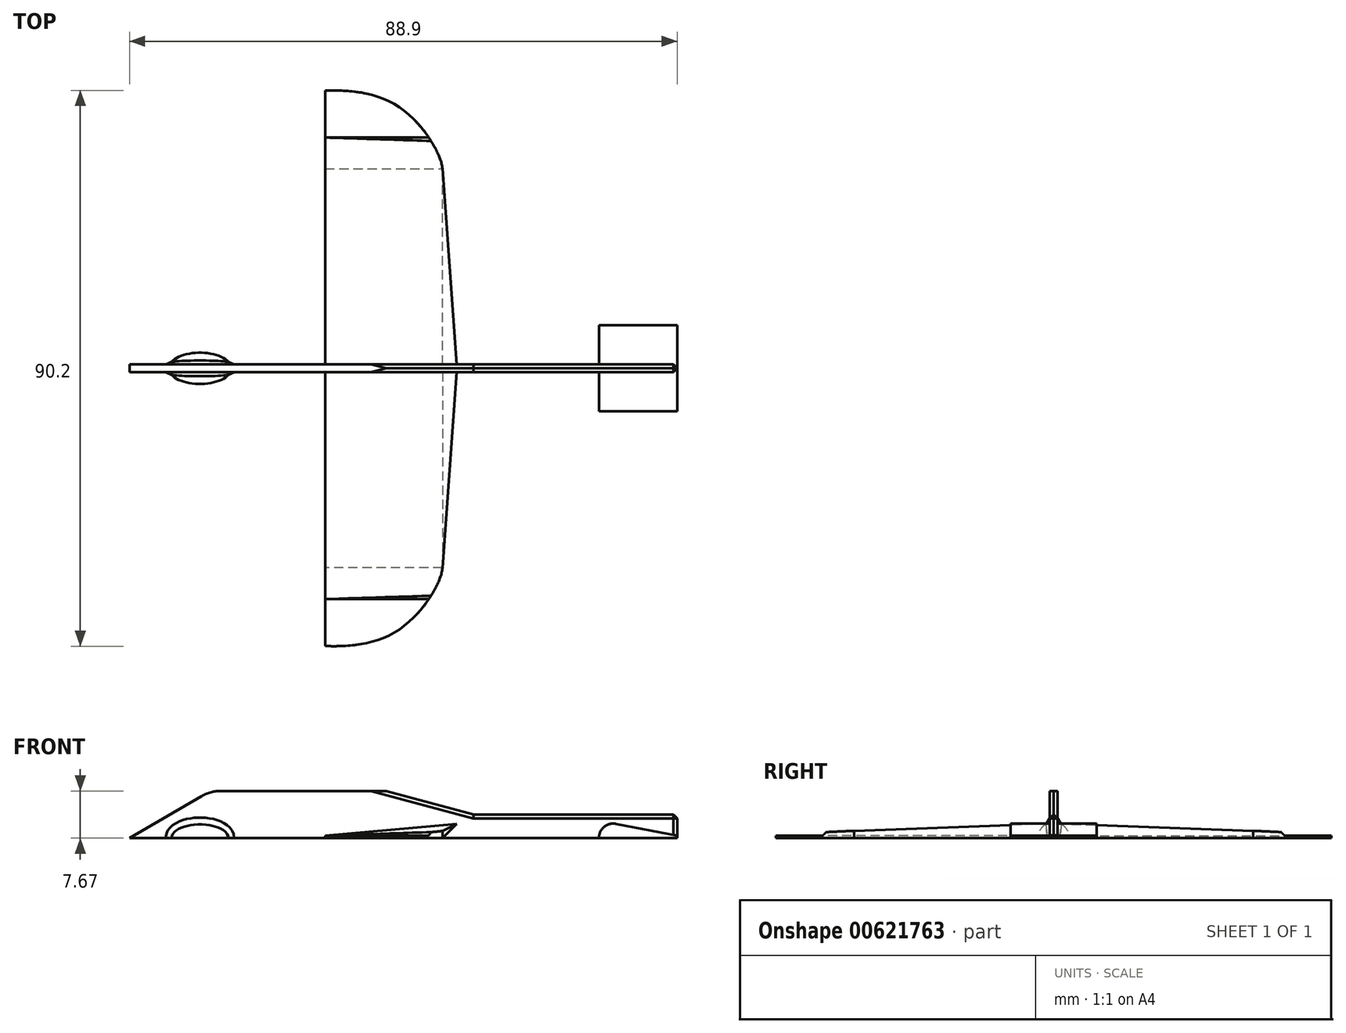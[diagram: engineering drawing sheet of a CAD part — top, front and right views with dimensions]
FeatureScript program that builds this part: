
annotation { "Feature Type Name" : "Feature", "Feature Type Description" : "" }
export const myFeature = defineFeature(function(context is Context, id is Id, definition is map)
    precondition{}
    {
        {
            var Q0;
            Q0=qCreatedBy(makeId("Front.planeOp"),FACE);
            cPlane(context, id + "F0", {"entities" : qUnion([Q0]), "cplaneType" : CPlaneType.OFFSET, "offset" : 0.64 * mm, "width" : 152.4 * mm, "height" : 152.4 * mm});
        }
        {
            var Q0;
            Q0=qCreatedBy(id+"F0.planeOp",FACE);
            var sketch = newSketch(context, id + "F1", { "sketchPlane" : qUnion([Q0])});
            skLineSegment(sketch, "E0", {"start": v(-19.05, 0) * mm, "end": v(0, 0) * mm});
            skLineSegment(sketch, "E1", {"start": v(0, 0) * mm, "end": v(2.29, 2.29) * mm});
            skLineSegment(sketch, "E2", {"start": v(-19.05, 0) * mm, "end": v(-19.05, 0.38) * mm});
            skLineSegment(sketch, "E3", {"start": v(-19.05, 0.38) * mm, "end": v(2.29, 2.29) * mm});
            skSolve(sketch);
        }
        {
            var Q0;
            Q0=qCreatedBy(id+"F0.planeOp",FACE);
            cPlane(context, id + "F2", {"entities" : qUnion([Q0]), "cplaneType" : CPlaneType.OFFSET, "offset" : 31.75 * mm, "width" : 152.4 * mm, "height" : 152.4 * mm});
        }
        {
            var Q0;
            Q0=qCreatedBy(id+"F2.planeOp",FACE);
            var sketch = newSketch(context, id + "F3", { "sketchPlane" : qUnion([Q0])});
            skLineSegment(sketch, "E4.bottom", {"start": v(0, 0) * mm, "end": v(-19.05, -0.05) * mm});
            skLineSegment(sketch, "E4.top", {"start": v(0, 1.14) * mm, "end": v(-19.05, 0.38) * mm});
            skLineSegment(sketch, "E4.left", {"start": v(0, 0) * mm, "end": v(0, 1.14) * mm});
            skLineSegment(sketch, "E4.right", {"start": v(-19.05, -0.05) * mm, "end": v(-19.05, 0.38) * mm});
            skSolve(sketch);
        }
        {
            var Q0;
            Q0 = qSketchRegion(id + "F1", true);
            var Q1;
            Q1 = qSketchRegion(id + "F3", true);
            loft(context, id + "F4", {"sheetProfilesArray" : [{ "sheetProfileEntities" : qUnion([Q0]) }, { "sheetProfileEntities" : qUnion([Q1]) }]});
        }
        {
            var Q0;
            Q0=qCreatedBy(makeId("Top.planeOp"),FACE);
            var sketch = newSketch(context, id + "F5", { "sketchPlane" : qUnion([Q0])});
            skLineSegment(sketch, "E5", {"start": v(-19.05, -32.38) * mm, "end": v(0, -32.38) * mm});
            skLineSegment(sketch, "E6", {"start": v(-19.05, -45.09) * mm, "end": v(-19.05, -32.38) * mm});
            skFitSpline(sketch, "E7", {"points": [v(-19.05, -45.09) * mm, v(-8.27, -43.16) * mm, v(0, -32.38) * mm], "startDerivative": vector(8.05, 0) * mm, "endDerivative": vector(1.04, 14.46) * mm});
            skLineSegment(sketch, "E8", {"start": v(-19.05, -45.09) * mm, "end": v(-21.64, -45.09) * mm, "construction": true});
            skLineSegment(sketch, "E9", {"start": v(-19.05, -32.38) * mm, "end": v(-8.27, -43.16) * mm, "construction": true});
            skSolve(sketch);
        }
        {
            var Q0;
            Q0 = qSketchRegion(id + "F5", true);
            var Q1;
            Q1=makeQuery(id+"F4.opLoft","MID_CAP_VERTEX",VERTEX,{"disambiguationData":[OSD([sQuery(id+"F3.wireOp",EDGE,"E4.top"),sQuery(id+"F3.wireOp",EDGE,"E4.right")])],"capPos":1.0});
            extrude(context, id + "F6", {"entities" : qUnion([Q0]), "operationType" : NewBodyOperationType.ADD, "endBound" : BoundingType.UP_TO_VERTEX, "depth" : 0.76 * mm, "endBoundEntityVertex" : qUnion([Q1]), "offsetDistance" : 25.4 * mm});
        }
        {
            var Q0;
            Q0=qCreatedBy(makeId("Front.planeOp"),FACE);
            var sketch = newSketch(context, id + "F7", { "sketchPlane" : qUnion([Q0])});
            skLineSegment(sketch, "E10", {"start": v(0, 0) * mm, "end": v(-50.8, 0) * mm});
            skLineSegment(sketch, "E11", {"start": v(-50.8, 0) * mm, "end": v(-39.08, 6.77) * mm});
            skLineSegment(sketch, "E12", {"start": v(-35.9, 7.62) * mm, "end": v(-9.14, 7.62) * mm});
            skLineSegment(sketch, "E13", {"start": v(38.1, 3.81) * mm, "end": v(38.1, 0) * mm});
            skLineSegment(sketch, "E14", {"start": v(38.1, 0) * mm, "end": v(0, 0) * mm});
            skPoint(sketch, "E15.visualSharp", {"position": v(-37.6, 7.62) * mm});
            skArc(sketch, "E15.filletArc", {"start": v(-35.9, 7.62) * mm, "mid": v(-37.54, 7.4) * mm, "end": v(-39.08, 6.77) * mm});
            skLineSegment(sketch, "E16", {"start": v(38.1, 3.81) * mm, "end": v(5.08, 3.8) * mm});
            skLineSegment(sketch, "E17", {"start": v(5.08, 3.8) * mm, "end": v(-9.14, 7.62) * mm});
            skSolve(sketch);
        }
        {
            var Q0;
            Q0 = qSketchRegion(id + "F7", true);
            var Q1;
            Q1=qCreatedBy(id+"F0.planeOp",FACE);
            extrude(context, id + "F8", {"entities" : qUnion([Q0]), "operationType" : NewBodyOperationType.ADD, "endBound" : BoundingType.UP_TO_SURFACE, "depth" : 25.4 * mm, "endBoundEntityFace" : qUnion([Q1]), "offsetDistance" : 25.4 * mm});
        }
        {
            var Q0;
            Q0=qCreatedBy(id+"F0.planeOp",FACE);
            var sketch = newSketch(context, id + "F9", { "sketchPlane" : qUnion([Q0])});
            skArc(sketch, "E18", {"start": v(28.17, 2.29) * mm, "mid": v(26.24, 1.8) * mm, "end": v(25.4, 0) * mm});
            skLineSegment(sketch, "E19", {"start": v(28.17, 2.29) * mm, "end": v(38.1, 0.38) * mm});
            skLineSegment(sketch, "E20", {"start": v(38.1, 0.38) * mm, "end": v(38.1, 0) * mm});
            skLineSegment(sketch, "E21", {"start": v(38.1, 0) * mm, "end": v(25.4, 0) * mm});
            skSolve(sketch);
        }
        {
            var Q0;
            Q0 = qSketchRegion(id + "F9", true);
            extrude(context, id + "F10", {"entities" : qUnion([Q0]), "operationType" : NewBodyOperationType.ADD, "depth" : 6.35 * mm, "offsetDistance" : 25.4 * mm});
        }
        {
            var Q0;
            Q0=makeQuery(id+"F4.opLoft","SWEPT_BODY",BODY,{"disambiguationData":[OSD([makeQuery(id+"F1.imprint","IMPRINT",FACE,{"disambiguationData":[TD([[makeQuery(id+"F1.imprint","IMPRINT",EDGE,{"derivedFrom":sQuery(id+"F1.wireOp",EDGE,"E0")}),1.0]])]}),makeQuery(id+"F3.imprint","IMPRINT",FACE,{"disambiguationData":[TD([[makeQuery(id+"F3.imprint","IMPRINT",EDGE,{"derivedFrom":sQuery(id+"F3.wireOp",EDGE,"E4.bottom")}),-1.0]])]})])]});
            var Q1;
            Q1=qCreatedBy(makeId("Front.planeOp"),FACE);
            mirror(context, id + "F11", {"operationType" : NewBodyOperationType.ADD, "entities" : qUnion([Q0]), "mirrorPlane" : qUnion([Q1])});
        }
        {
            var Q0;
            Q0=makeQuery(id+"F11.opPattern","COPY",EDGE,{"derivedFrom":makeQuery(id+"F8.opExtrude","CAP_EDGE",EDGE,{"disambiguationData":[OSD([sQuery(id+"F7.wireOp",EDGE,"E17")])],"isStart":false}),"instanceName":"1"});
            var Q1;
            Q1=makeQuery(id+"F8.opExtrude","CAP_EDGE",EDGE,{"disambiguationData":[OSD([sQuery(id+"F7.wireOp",EDGE,"E17")])],"isStart":false});
            var Q2;
            Q2=makeQuery(id+"F11.opPattern","COPY",EDGE,{"derivedFrom":makeQuery(id+"F8.opExtrude","CAP_EDGE",EDGE,{"disambiguationData":[OSD([sQuery(id+"F7.wireOp",EDGE,"E16")])],"isStart":false}),"instanceName":"1"});
            var Q3;
            Q3=makeQuery(id+"F8.opExtrude","CAP_EDGE",EDGE,{"disambiguationData":[OSD([sQuery(id+"F7.wireOp",EDGE,"E16")])],"isStart":false});
            var Q4;
            {var subQ0=makeQuery(id+"F8.opExtrude","SWEPT_EDGE",EDGE,{"disambiguationData":[OSD([sQuery(id+"F7.wireOp",EDGE,"E13"),sQuery(id+"F7.wireOp",EDGE,"E16")])]});Q4=makeQuery(id+"F11.boolean.opBoolean","MERGE",EDGE,{"derivedFrom":[subQ0,makeQuery(id+"F11.opPattern","COPY",EDGE,{"derivedFrom":subQ0,"instanceName":"1"})]});}
            var Q5;
            Q5=makeQuery(id+"F11.opPattern","COPY",EDGE,{"derivedFrom":makeQuery(id+"F8.opExtrude","CAP_EDGE",EDGE,{"disambiguationData":[OSD([sQuery(id+"F7.wireOp",EDGE,"E13")])],"isStart":false}),"instanceName":"1"});
            var Q6;
            Q6=makeQuery(id+"F8.opExtrude","CAP_EDGE",EDGE,{"disambiguationData":[OSD([sQuery(id+"F7.wireOp",EDGE,"E13")])],"isStart":false});
            chamfer(context, id + "F12", {"entities" : qUnion([Q0, Q1, Q2, Q3, Q4, Q5, Q6]), "width" : 0.64 * mm, "tangentPropagation" : true});
        }
        {
            var Q0;
            Q0=makeQuery(id+"F6.opExtrude","CAP_EDGE",EDGE,{"disambiguationData":[OSD([sQuery(id+"F5.wireOp",EDGE,"E5")])],"isStart":false});
            var Q1;
            Q1=makeQuery(id+"F11.opPattern","COPY",EDGE,{"derivedFrom":makeQuery(id+"F6.opExtrude","CAP_EDGE",EDGE,{"disambiguationData":[OSD([sQuery(id+"F5.wireOp",EDGE,"E5")])],"isStart":false}),"instanceName":"1"});
            chamfer(context, id + "F13", {"entities" : qUnion([Q0, Q1]), "width" : 5.08 * mm, "tangentPropagation" : true});
        }
        {
            var Q0;
            Q0=qCreatedBy(makeId("Top.planeOp"),FACE);
            var sketch = newSketch(context, id + "F14", { "sketchPlane" : qUnion([Q0])});
            skLineSegment(sketch, "E22", {"start": v(-44.45, 0) * mm, "end": v(-34.29, 0) * mm});
            skEllipticalArc(sketch, "E23", {});
            skPoint(sketch, "E24", {"position": v(-39.37, -2.54) * mm});
            const initialGuessF14  = {"E23": [-0.03937, 0, -1, 0, 0.00508, 0.00254, 0, 3.141592653589793]};
            skSetInitialGuess(sketch, initialGuessF14);
            skSolve(sketch);
        }
        {
            var Q0;
            Q0 = qSketchRegion(id + "F14", true);
            var Q1;
            Q1=sQuery(id+"F14.wireOp",EDGE,"E22");
            revolve(context, id + "F15", {"operationType" : NewBodyOperationType.ADD, "entities" : qUnion([Q0]), "axis" : qUnion([Q1]), "revolveType" : RevolveType.ONE_DIRECTION, "oppositeDirection" : true, "angle" : 180 * degree});
        }
        {
            var Q0;
            Q0=makeQuery(id+"F15.boolean.opBoolean","INTERSECT",EDGE,{"derivedFrom":[makeQuery(id+"F8.opExtrude","CAP_FACE",FACE,{"disambiguationData":[OSD([sQuery(id+"F7.wireOp",EDGE,"E10"),sQuery(id+"F7.wireOp",EDGE,"E11"),sQuery(id+"F7.wireOp",EDGE,"E12"),sQuery(id+"F7.wireOp",EDGE,"E13"),sQuery(id+"F7.wireOp",EDGE,"E14"),sQuery(id+"F7.wireOp",EDGE,"E15.filletArc"),sQuery(id+"F7.wireOp",EDGE,"E16"),sQuery(id+"F7.wireOp",EDGE,"E17")])],"isStart":false}),makeQuery(id+"F15.opRevolve","SWEPT_FACE",FACE,{"disambiguationData":[OSD([sQuery(id+"F14.wireOp",EDGE,"E23")])]})]});
            var Q1;
            Q1=makeQuery(id+"F15.boolean.opBoolean","INTERSECT",EDGE,{"derivedFrom":[makeQuery(id+"F11.opPattern","COPY",FACE,{"derivedFrom":makeQuery(id+"F8.opExtrude","CAP_FACE",FACE,{"disambiguationData":[OSD([sQuery(id+"F7.wireOp",EDGE,"E10"),sQuery(id+"F7.wireOp",EDGE,"E11"),sQuery(id+"F7.wireOp",EDGE,"E12"),sQuery(id+"F7.wireOp",EDGE,"E13"),sQuery(id+"F7.wireOp",EDGE,"E14"),sQuery(id+"F7.wireOp",EDGE,"E15.filletArc"),sQuery(id+"F7.wireOp",EDGE,"E16"),sQuery(id+"F7.wireOp",EDGE,"E17")])],"isStart":false}),"instanceName":"1"}),makeQuery(id+"F15.opRevolve","SWEPT_FACE",FACE,{"disambiguationData":[OSD([sQuery(id+"F14.wireOp",EDGE,"E23")])]})]});
            chamfer(context, id + "F16", {"entities" : qUnion([Q0, Q1]), "width" : 1.27 * mm, "tangentPropagation" : true});
        }
    });
